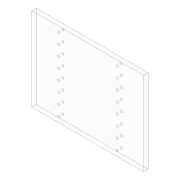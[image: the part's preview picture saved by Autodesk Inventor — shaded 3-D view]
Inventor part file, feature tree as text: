
AUTODESK INVENTOR PART (.ipt)
format: ipt  version: 2018 (Build 220112000, 112)  size: 102,400 bytes
history: native  units: mm
features: sketch x2, extrude x1, hole x1, pattern_linear x1, projected_geometry x1
ambient origin geometry x8: Origin, YZ Plane, XZ Plane, XY Plane, X Axis, Y Axis, Z Axis, Center Point
bodies: Solid1 (feature_tree)
feature tree (6):
  extrude  "Extrusion1"  Depth=112.0mm
  hole  "Hole1"  [1 undecoded]
  pattern_linear  "Rectangular Pattern1"  Spacing1=7.0mm  [1 undecoded]
  sketch  "Sketch1"  dims[d0=150.0mm d1=112.0mm]
  sketch  "Sketch2"  dims[d2=6.0mm d3=0.0mm d4=78.4mm d6=2.9mm d7=3.708mm d8=5.5mm d9=1.524mm d10=90.0deg d11=8.0mm d12=20.594885mm d13=7.0mm d14=39.2mm d15=80.0mm d17=14.0mm]
  projected_geometry  "Projected Loop1"
note: 2 required parameter values undecoded (feature->parameter linkage not recoverable at this tier; creation-order binding heuristic only, values carry confidence <= 0.55)
